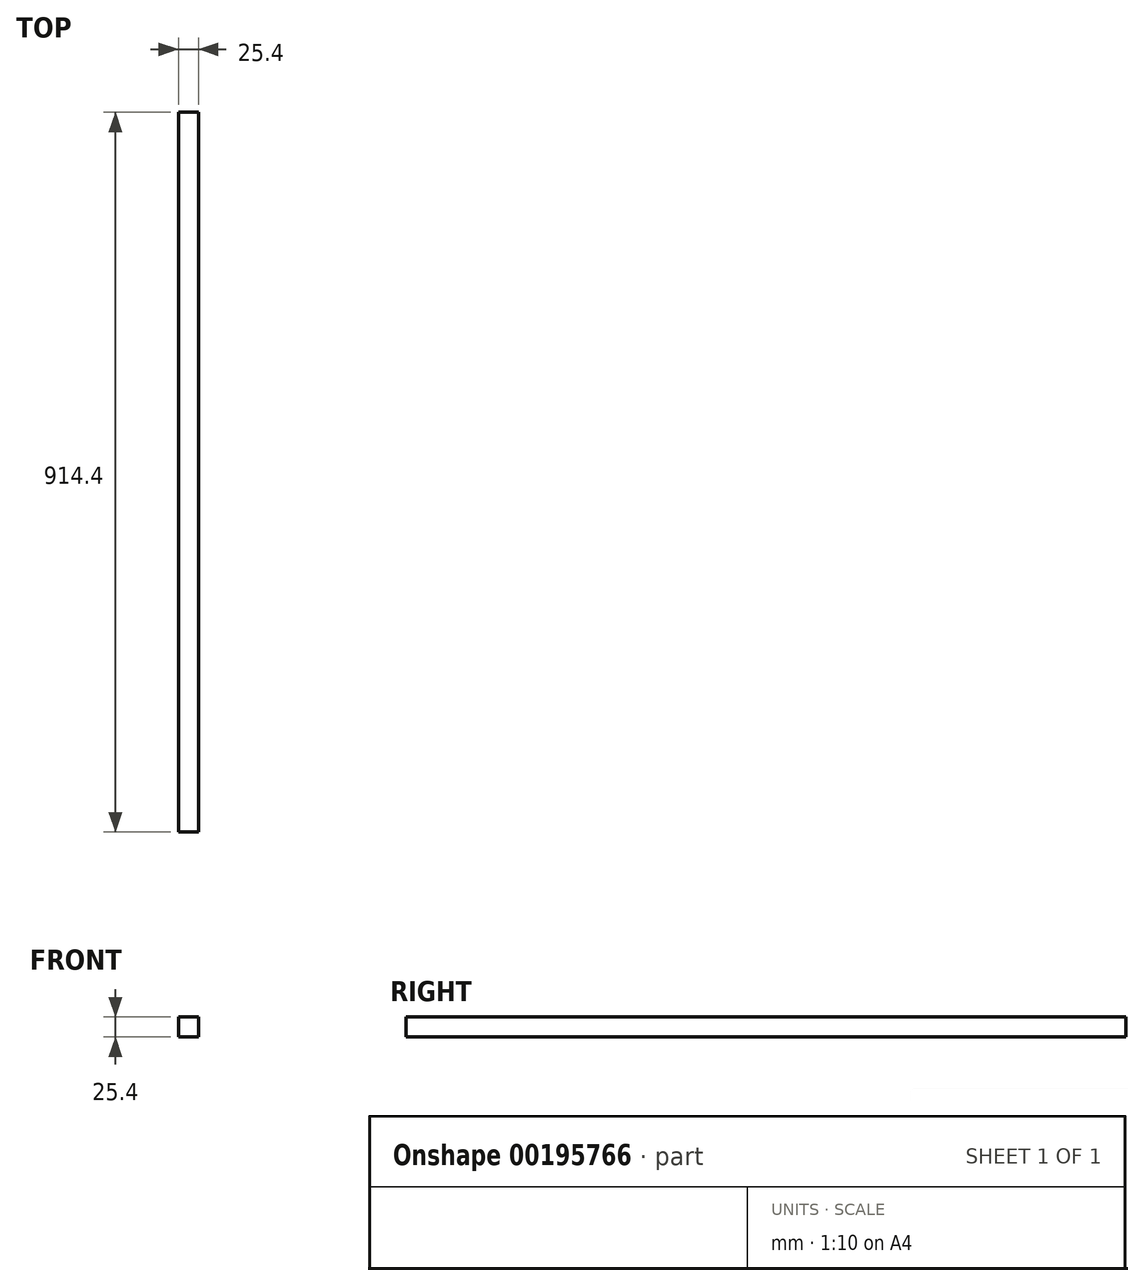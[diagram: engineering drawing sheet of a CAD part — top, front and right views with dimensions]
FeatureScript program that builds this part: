
annotation { "Feature Type Name" : "Feature", "Feature Type Description" : "" }
export const myFeature = defineFeature(function(context is Context, id is Id, definition is map)
    precondition{}
    {
        {
            var Q0;
            Q0=qCreatedBy(makeId("Front.planeOp"),FACE);
            var sketch = newSketch(context, id + "F0", { "sketchPlane" : qUnion([Q0])});
            skLineSegment(sketch, "E0.bottom", {"start": v(0, 0) * mm, "end": v(25.4, 0) * mm});
            skLineSegment(sketch, "E0.top", {"start": v(0, 25.4) * mm, "end": v(25.4, 25.4) * mm});
            skLineSegment(sketch, "E0.left", {"start": v(0, 0) * mm, "end": v(0, 25.4) * mm});
            skLineSegment(sketch, "E0.right", {"start": v(25.4, 0) * mm, "end": v(25.4, 25.4) * mm});
            skSolve(sketch);
        }
        {
            var Q0;
            Q0=makeQuery(id+"F0.imprint","IMPRINT",FACE,{"disambiguationData":[TD([[makeQuery(id+"F0.imprint","IMPRINT",EDGE,{"derivedFrom":sQuery(id+"F0.wireOp",EDGE,"E0.bottom")}),1.0]])]});
            extrude(context, id + "F1", {"entities" : qUnion([Q0]), "depth" : 914.4 * mm});
        }
    });
